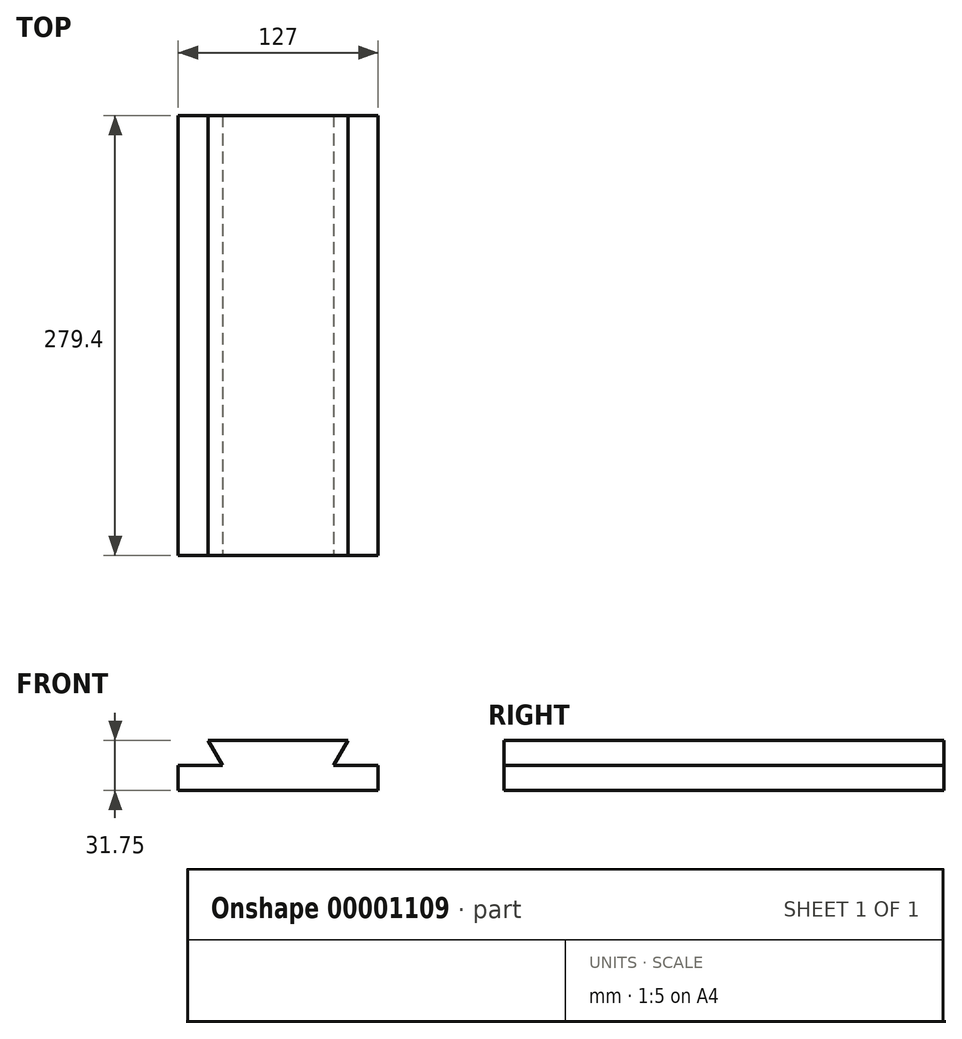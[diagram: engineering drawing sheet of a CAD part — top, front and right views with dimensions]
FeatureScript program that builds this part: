
annotation { "Feature Type Name" : "Feature", "Feature Type Description" : "" }
export const myFeature = defineFeature(function(context is Context, id is Id, definition is map)
    precondition{}
    {
        {
            var Q0;
            Q0=qCreatedBy(makeId("Front.planeOp"),FACE);
            var sketch = newSketch(context, id + "F0", { "sketchPlane" : qUnion([Q0])});
            skLineSegment(sketch, "E0", {"start": v(-63.5, 0) * mm, "end": v(-63.5, 15.87) * mm});
            skLineSegment(sketch, "E1", {"start": v(-63.5, 15.87) * mm, "end": v(-35.28, 15.87) * mm});
            skLineSegment(sketch, "E2", {"start": v(-35.28, 15.87) * mm, "end": v(-44.45, 31.75) * mm});
            skLineSegment(sketch, "E3", {"start": v(-44.45, 31.75) * mm, "end": v(44.45, 31.75) * mm});
            skLineSegment(sketch, "E4", {"start": v(44.45, 31.75) * mm, "end": v(35.28, 15.87) * mm});
            skLineSegment(sketch, "E5", {"start": v(35.28, 15.87) * mm, "end": v(63.5, 15.87) * mm});
            skLineSegment(sketch, "E6", {"start": v(63.5, 15.87) * mm, "end": v(63.5, 0) * mm});
            skLineSegment(sketch, "E7", {"start": v(63.5, 0) * mm, "end": v(-63.5, 0) * mm});
            skSolve(sketch);
        }
        {
            var Q0;
            Q0=makeQuery(id+"F0.imprint","IMPRINT",FACE,{"disambiguationData":[TD([[makeQuery(id+"F0.imprint","IMPRINT",EDGE,{"derivedFrom":sQuery(id+"F0.wireOp",EDGE,"E0")}),-1.0]])]});
            extrude(context, id + "F1", {"entities" : qUnion([Q0]), "oppositeDirection" : true, "depth" : 279.4 * mm});
        }
    });
